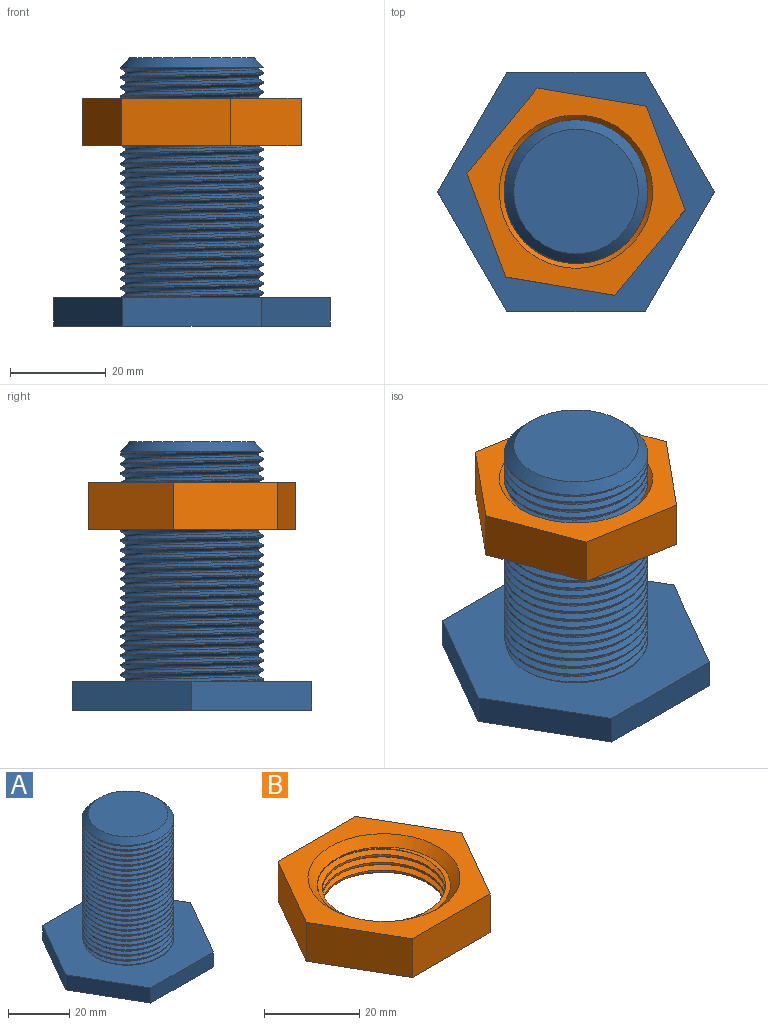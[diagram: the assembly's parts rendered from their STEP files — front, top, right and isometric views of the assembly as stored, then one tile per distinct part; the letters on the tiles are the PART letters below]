
ASSEMBLY  parts=2 mates=1
PART A: 15 faces, bbox 58.3x50.6x56.6 mm
  f0: plane 28.87x6mm, normal (0,1,0), area 173.2mm2, adj f1,f5,f6,f7
  f1: plane 25x14.43mm, normal (-0.87,0.5,0), area 173.2mm2, adj f0,f2,f6,f7
  f2: plane 25x14.43mm, normal (-0.87,-0.5,0), area 173.2mm2, adj f1,f3,f6,f7
  f3: plane 28.87x6mm, normal (0,-1,0), area 173.2mm2, adj f2,f4,f6,f7
  f4: plane 25x14.43mm, normal (0.87,-0.5,0), area 173.2mm2, adj f3,f5,f6,f7
  f5: plane 25x14.43mm, normal (0.87,0.5,0), area 173.2mm2, adj f0,f4,f6,f7
  f6: plane 58.33x50.59mm, normal (0,0,1), area 1515.6mm2, adj f0,f1,f2,f3,f4,f5,f8,f11
  f7: plane 57.74x50mm, normal (0,0,-1), area 2165.1mm2, adj f0,f1,f2,f3,f4,f5
  f8: cylinder r=15mm len=48mm, axis (0,0,-1), area 378.6mm2, adj f6,f10,f12,f13
  f9: plane 26x26mm, normal (0,0,1), area 530.9mm2, adj f10
  f10: cone r=13mm half-angle=45deg, axis (0,0,-1), area 248.8mm2, adj f8,f9,f14
  f11: bspline ~49.5x32.14mm, area 1168mm2, adj f6,f12,f13,f14
  f12: bspline ~49.63x34.64mm, area 2724.8mm2, adj f6,f8,f11,f14
  f13: bspline ~49.29x34.64mm, area 2730.3mm2, adj f6,f8,f11,f14
  f14: plane 30.59x30.59mm, normal (0,0,-1), area 57.3mm2, adj f10,f11,f12,f13
PART B: 18 faces, bbox 46.8x40.6x10.6 mm
  f0: plane 23.09x10mm, normal (0,1,0), area 230.9mm2, adj f1,f5,f6,f7
  f1: plane 20x11.55mm, normal (-0.87,0.5,0), area 230.9mm2, adj f0,f2,f6,f7
  f2: plane 20x11.55mm, normal (-0.87,-0.5,0), area 230.9mm2, adj f1,f3,f6,f7
  f3: plane 23.09x10mm, normal (0,-1,0), area 230.9mm2, adj f2,f4,f6,f7
  f4: plane 20x11.55mm, normal (0.87,-0.5,0), area 230.9mm2, adj f3,f5,f6,f7
  f5: plane 20x11.55mm, normal (0.87,0.5,0), area 230.9mm2, adj f0,f4,f6,f7
  f6: plane 46.19x40mm, normal (0,0,1), area 581.4mm2, adj f0,f1,f2,f3,f4,f5,f9
  f7: plane 46.19x40mm, normal (0,0,-1), area 581.4mm2, adj f0,f1,f2,f3,f4,f5,f8
  f8: cone r=16mm half-angle=45deg, axis (0,0,-1), area 266.6mm2, adj f7,f13,f15
  f9: cone r=14mm half-angle=45deg, axis (0,0,1), area 266.6mm2, adj f6,f14,f16
  f10: bspline ~32.52x28.17mm, area 319.2mm2, adj f12,f13,f14,f15,f16,f17
  f11: bspline ~32.52x28.17mm, area 319.2mm2, adj f12,f13,f14,f15,f16,f17
  f12: bspline ~32.73x28.35mm, area 77.1mm2, adj f10,f11,f13,f14
  f13: plane 10.54x10.36mm, normal (0,0,1), area 1.6mm2, adj f8,f10,f11,f12
  f14: plane 10.54x10.36mm, normal (0,0,-1), area 1.6mm2, adj f9,f10,f11,f12
  f15: plane 28.59x28.59mm, normal (0,0,-1), area 46mm2, adj f8,f10,f11,f17
  f16: plane 28.59x28.59mm, normal (0,0,1), area 46mm2, adj f9,f10,f11,f17
  f17: cylinder r=13mm len=26mm, axis (0,0,-1), area 122.9mm2, adj f10,f11,f15,f16
PLACE A t=(-22.83,-10.33,-1.54)mm fixed
PLACE B rot(axis=(0,0,1),50.5deg) t=(13.47,33.63,36.09)mm
MATE cylindrical A.f8 <-> B.f8  axis (0,0,1) through (-22.83,-10.33,54.46)mm
